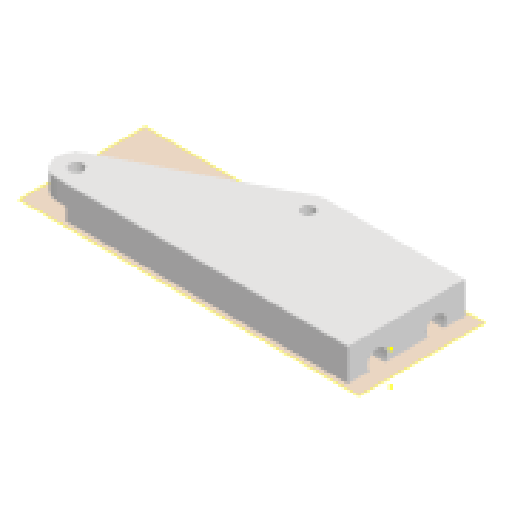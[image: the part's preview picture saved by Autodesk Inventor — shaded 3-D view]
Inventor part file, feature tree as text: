
AUTODESK INVENTOR PART (.ipt)
format: ipt  version: 2024 (Build 280153000, 153)  size: 256,000 bytes
history: native  units: mm
features: sketch x10, extrude x9, fillet x6, plane x3
ambient origin geometry x8: Origin, YZ Plane, XZ Plane, XY Plane, X Axis, Y Axis, Z Axis, Center Point
bodies: Solid1 (feature_tree)
feature tree (28):
  sketch  "Sketch1"  dims[d0=10.0mm d1=10.0mm d3=59.4mm]
  extrude  "Extrusion1"  Depth=10.0mm
  fillet  "Fillet1"  Radius=59.4mm
  extrude  "Extrusion2"  Depth=15.0mm
  sketch  "Sketch4"  dims[d6=15.0mm d7=15.0mm]
  extrude  "Extrusion5"  Depth=15.0mm
  extrude  "Extrusion6"  Depth=15.0mm
  fillet  "Fillet3"  Radius=15.0mm
  sketch  "Sketch5"  dims[d8=40.0mm d9=0.0mm d10=15.0mm d12=15.0mm]
  extrude  "Extrusion7"  Depth=15.0mm
  extrude  "Extrusion8"  Depth=30.0mm TaperAngle=0.0deg
  sketch  "Sketch7"  dims[d13=22.35mm d14=15.0mm]
  plane  "Work Plane1"
  extrude  "Extrusion9"  Depth=25.0mm TaperAngle=0.0deg
  plane  "Work Plane2"
  extrude  "Extrusion10"  Depth=116.1mm
  fillet  "Fillet4"  Radius=105.0mm
  fillet  "Fillet5"  Radius=283.350776mm
  fillet  "Fillet6"  Radius=1.0mm
  fillet  "Fillet7"  Radius=22.0mm
  sketch  "Sketch10"  dims[d28=15.0mm d29=0.0mm d32=116.1mm d33=105.0mm d34=283.350776mm d35=1.0mm d36=22.0mm]
  plane  "Work Plane3"
  sketch  "Sketch13"  dims[d37=20.495401mm d38=25.0mm d39=0.0mm]
  extrude  "Extrusion11"  Depth=25.0mm TaperAngle=0.0deg
  sketch  "Sketch2"  dims[d4=89.4mm d5=15.0mm]
  sketch  "Sketch8"  dims[d15=22.35mm d16=30.0mm d17=0.0mm]
  sketch  "Sketch9"  dims[d23=19.010126mm d26=25.0mm d27=0.0mm]
  sketch  "Sketch14"  dims[d40=15.0mm d41=0.0mm d44=90.0deg d45=26.5mm d46=28.0mm d47=0.0mm d48=90.0deg d49=26.0mm d50=18.0mm d51=0.0mm d52=5.0mm d53=5.0mm d54=5.0mm d55=5.0mm d56=-25.0mm d59=-1.594mm d60=-3.599316mm d61=-3.810496mm d62=-3.050618mm d63=0.0mm d64=0.0mm d42=0.5mm d43=0.872665mm d57=0.0mm d58=0.872665mm]
